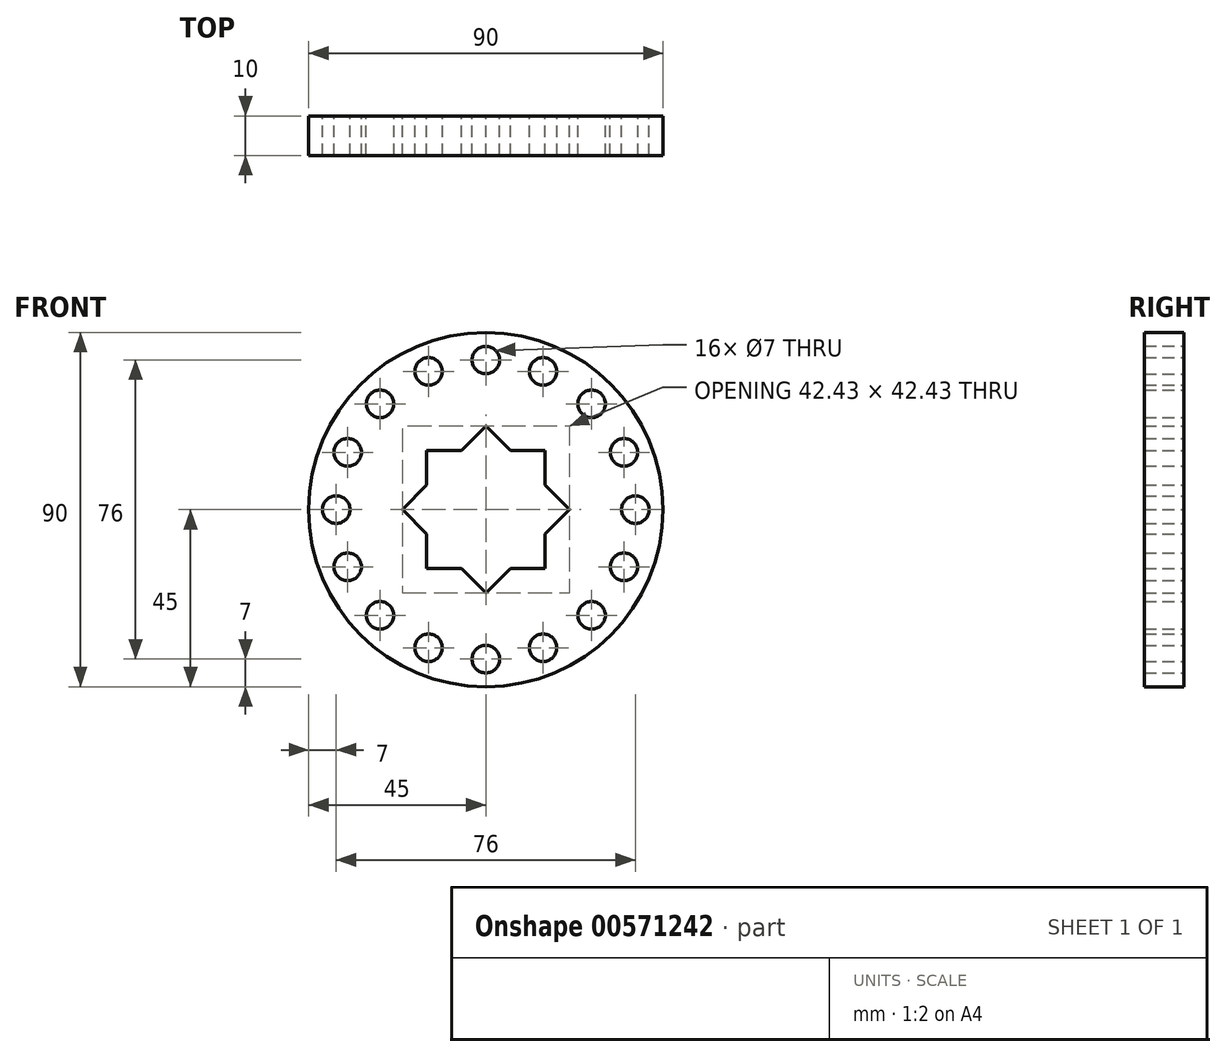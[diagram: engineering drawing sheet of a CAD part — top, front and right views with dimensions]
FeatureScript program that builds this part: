
annotation { "Feature Type Name" : "Feature", "Feature Type Description" : "" }
export const myFeature = defineFeature(function(context is Context, id is Id, definition is map)
    precondition{}
    {
        {
            var Q0;
            Q0=qCreatedBy(makeId("Front.planeOp"),FACE);
            var sketch = newSketch(context, id + "F0", { "sketchPlane" : qUnion([Q0])});
            skCircle(sketch, "E0", {"center": v(0, 0) * mm, "radius": 45 * mm});
            skCircle(sketch, "E1", {"center": v(0, 0) * mm, "radius": 38 * mm, "construction": true});
            skCircle(sketch, "E2", {"center": v(0, 38) * mm, "radius": 3.5 * mm});
            skCircle(sketch, "E3.1.0", {"center": v(-14.54, 35.1) * mm, "radius": 3.5 * mm});
            skCircle(sketch, "E3.2.0", {"center": v(-26.87, 26.87) * mm, "radius": 3.5 * mm});
            skCircle(sketch, "E4.1.3.0", {"center": v(-35.1, 14.54) * mm, "radius": 3.5 * mm});
            skCircle(sketch, "E4.1.4.0", {"center": v(-38, 0) * mm, "radius": 3.5 * mm});
            skCircle(sketch, "E4.1.5.0", {"center": v(-35.1, -14.54) * mm, "radius": 3.5 * mm});
            skCircle(sketch, "E4.1.6.0", {"center": v(-26.87, -26.87) * mm, "radius": 3.5 * mm});
            skCircle(sketch, "E4.1.7.0", {"center": v(-14.54, -35.1) * mm, "radius": 3.5 * mm});
            skCircle(sketch, "E4.1.8.0", {"center": v(0, -38) * mm, "radius": 3.5 * mm});
            skCircle(sketch, "E4.1.9.0", {"center": v(14.54, -35.1) * mm, "radius": 3.5 * mm});
            skCircle(sketch, "E4.1.10.0", {"center": v(26.87, -26.87) * mm, "radius": 3.5 * mm});
            skCircle(sketch, "E4.1.11.0", {"center": v(35.1, -14.54) * mm, "radius": 3.5 * mm});
            skCircle(sketch, "E4.1.12.0", {"center": v(38, 0) * mm, "radius": 3.5 * mm});
            skCircle(sketch, "E4.1.13.0", {"center": v(35.1, 14.54) * mm, "radius": 3.5 * mm});
            skCircle(sketch, "E4.1.14.0", {"center": v(26.87, 26.87) * mm, "radius": 3.5 * mm});
            skCircle(sketch, "E4.1.15.0", {"center": v(14.54, 35.1) * mm, "radius": 3.5 * mm});
            skCircle(sketch, "E5.cCircle", {"center": v(0, 0) * mm, "radius": 15 * mm, "construction": true});
            skLineSegment(sketch, "E5.0", {"start": v(21.21, 0) * mm, "end": v(0, -21.21) * mm});
            skLineSegment(sketch, "E5.1", {"start": v(0, -21.21) * mm, "end": v(-21.21, 0) * mm});
            skLineSegment(sketch, "E5.2", {"start": v(-21.21, 0) * mm, "end": v(0, 21.21) * mm});
            skLineSegment(sketch, "E5.3", {"start": v(0, 21.21) * mm, "end": v(21.21, 0) * mm});
            skPoint(sketch, "E5.0.midPoint", {"position": v(10.6, -10.6) * mm});
            skLineSegment(sketch, "E6.0", {"start": v(15, 15) * mm, "end": v(15, -15) * mm});
            skLineSegment(sketch, "E6.1", {"start": v(15, -15) * mm, "end": v(-15, -15) * mm});
            skLineSegment(sketch, "E6.2", {"start": v(-15, -15) * mm, "end": v(-15, 15) * mm});
            skLineSegment(sketch, "E6.3", {"start": v(-15, 15) * mm, "end": v(15, 15) * mm});
            skPoint(sketch, "E6.0.midPoint", {"position": v(15, 0) * mm});
            skSolve(sketch);
        }
        {
            var Q0;
            Q0=makeQuery(id+"F0.imprint","IMPRINT",FACE,{"disambiguationData":[TD([[makeQuery(id+"F0.imprint","IMPRINT",EDGE,{"derivedFrom":sQuery(id+"F0.wireOp",EDGE,"E0")}),1.0]])]});
            extrude(context, id + "F1", {"entities" : qUnion([Q0]), "depth" : 10 * mm, "offsetDistance" : 25 * mm});
        }
    });
